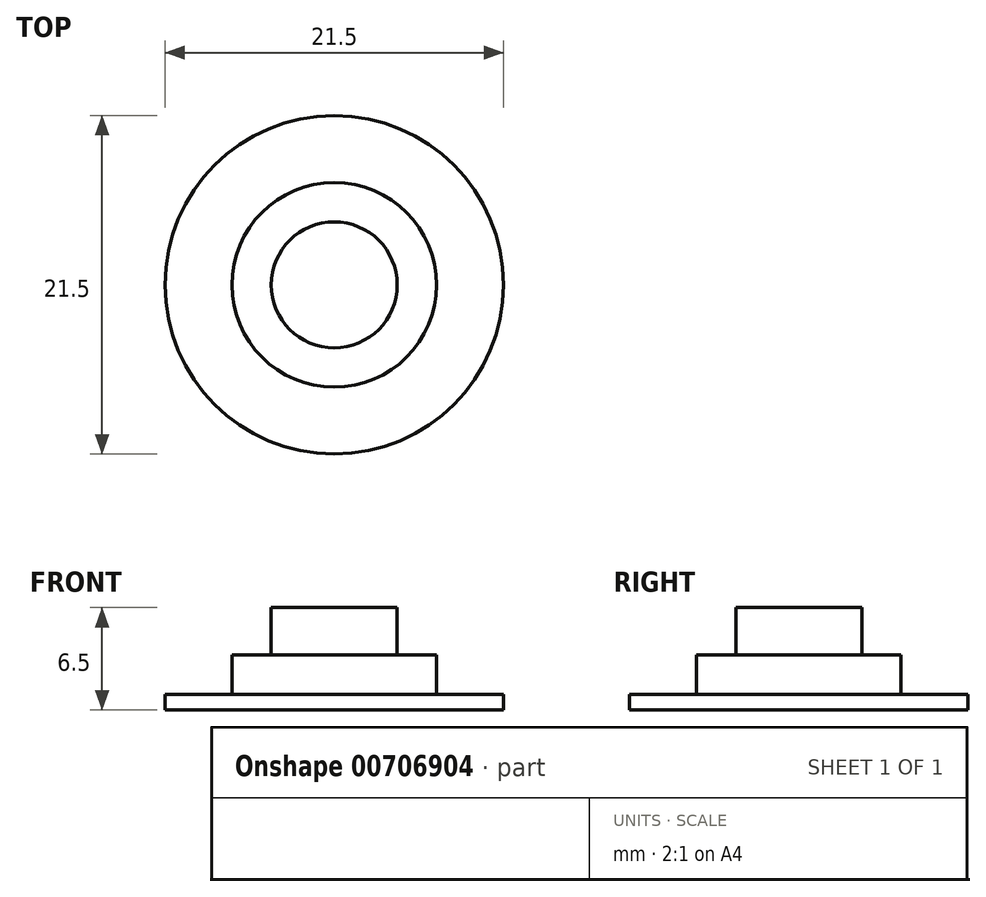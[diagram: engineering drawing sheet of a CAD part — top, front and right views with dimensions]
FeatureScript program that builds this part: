
annotation { "Feature Type Name" : "Feature", "Feature Type Description" : "" }
export const myFeature = defineFeature(function(context is Context, id is Id, definition is map)
    precondition{}
    {
        {
            var Q0;
            Q0=qCreatedBy(makeId("Top.planeOp"),FACE);
            var sketch = newSketch(context, id + "F0", { "sketchPlane" : qUnion([Q0])});
            skCircle(sketch, "E0", {"center": v(0, 0) * mm, "radius": 10.75 * mm});
            skCircle(sketch, "E1", {"center": v(0, 0) * mm, "radius": 6.5 * mm});
            skCircle(sketch, "E2", {"center": v(0, 0) * mm, "radius": 4 * mm});
            skSolve(sketch);
        }
        {
            var Q0;
            Q0=makeQuery(id+"F0.imprint","IMPRINT",FACE,{"disambiguationData":[TD([[makeQuery(id+"F0.imprint","IMPRINT",EDGE,{"derivedFrom":sQuery(id+"F0.wireOp",EDGE,"E0")}),1.0]])]});
            var Q1;
            Q1=makeQuery(id+"F0.imprint","IMPRINT",FACE,{"disambiguationData":[TD([[makeQuery(id+"F0.imprint","IMPRINT",EDGE,{"derivedFrom":sQuery(id+"F0.wireOp",EDGE,"E1")}),1.0]])]});
            var Q2;
            Q2=makeQuery(id+"F0.imprint","IMPRINT",FACE,{"disambiguationData":[TD([[makeQuery(id+"F0.imprint","IMPRINT",EDGE,{"derivedFrom":sQuery(id+"F0.wireOp",EDGE,"E2")}),1.0]])]});
            extrude(context, id + "F1", {"entities" : qUnion([Q0, Q1, Q2]), "depth" : 1 * mm, "offsetDistance" : 25.4 * mm});
        }
        {
            var Q0;
            Q0=makeQuery(id+"F0.imprint","IMPRINT",FACE,{"disambiguationData":[TD([[makeQuery(id+"F0.imprint","IMPRINT",EDGE,{"derivedFrom":sQuery(id+"F0.wireOp",EDGE,"E1")}),1.0]])]});
            var Q1;
            Q1=makeQuery(id+"F0.imprint","IMPRINT",FACE,{"disambiguationData":[TD([[makeQuery(id+"F0.imprint","IMPRINT",EDGE,{"derivedFrom":sQuery(id+"F0.wireOp",EDGE,"E2")}),1.0]])]});
            extrude(context, id + "F2", {"entities" : qUnion([Q0, Q1]), "operationType" : NewBodyOperationType.ADD, "depth" : 3.5 * mm, "offsetDistance" : 25.4 * mm});
        }
        {
            var Q0;
            Q0=makeQuery(id+"F0.imprint","IMPRINT",FACE,{"disambiguationData":[TD([[makeQuery(id+"F0.imprint","IMPRINT",EDGE,{"derivedFrom":sQuery(id+"F0.wireOp",EDGE,"E2")}),1.0]])]});
            extrude(context, id + "F3", {"entities" : qUnion([Q0]), "operationType" : NewBodyOperationType.ADD, "depth" : 6.5 * mm, "offsetDistance" : 25.4 * mm});
        }
    });
